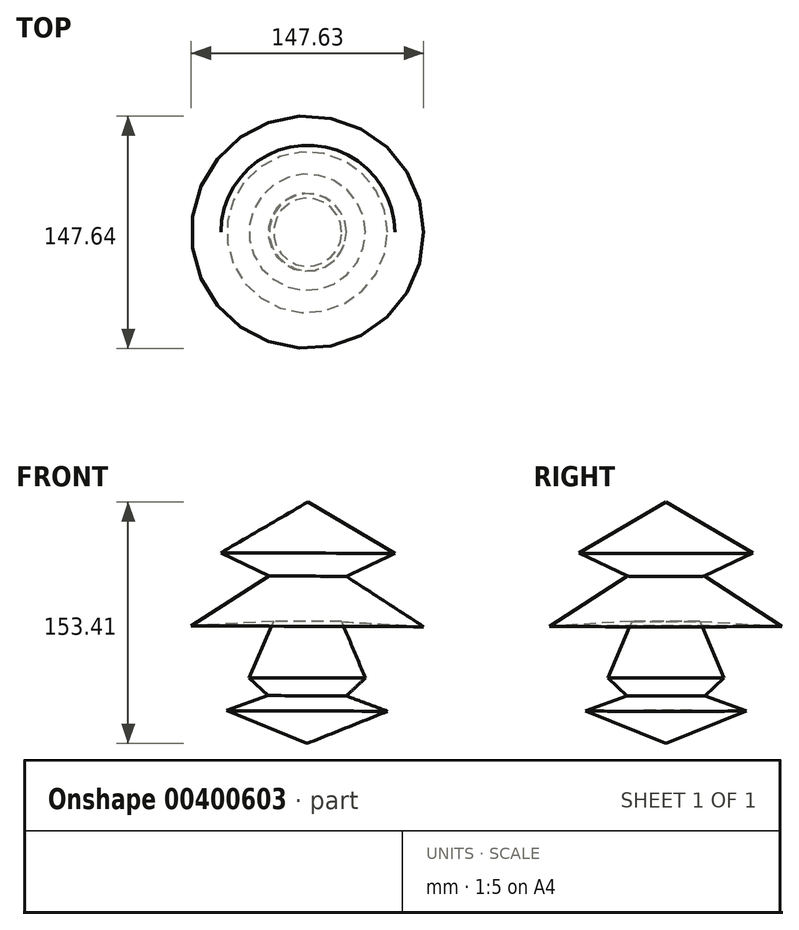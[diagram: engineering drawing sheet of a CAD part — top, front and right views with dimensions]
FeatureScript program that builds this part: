
annotation { "Feature Type Name" : "Feature", "Feature Type Description" : "" }
export const myFeature = defineFeature(function(context is Context, id is Id, definition is map)
    precondition{}
    {
        {
            var Q0;
            Q0=qCreatedBy(makeId("Front.planeOp"),FACE);
            var sketch = newSketch(context, id + "F0", { "sketchPlane" : qUnion([Q0])});
            skLineSegment(sketch, "E0", {"start": v(-14.32, 75.97) * mm, "end": v(40.82, 43.27) * mm});
            skLineSegment(sketch, "E1", {"start": v(40.82, 43.27) * mm, "end": v(9.99, 28.74) * mm});
            skLineSegment(sketch, "E2", {"start": v(9.99, 28.74) * mm, "end": v(59.2, -3.3) * mm});
            skLineSegment(sketch, "E3", {"start": v(59.2, -3.3) * mm, "end": v(7.03, 0) * mm});
            skLineSegment(sketch, "E4", {"start": v(7.03, 0) * mm, "end": v(22.14, -35.92) * mm});
            skLineSegment(sketch, "E5", {"start": v(22.14, -35.92) * mm, "end": v(9.99, -47.22) * mm});
            skLineSegment(sketch, "E6", {"start": v(9.99, -47.22) * mm, "end": v(38.15, -57.68) * mm});
            skLineSegment(sketch, "E7", {"start": v(36.25, -56.98) * mm, "end": v(-14.9, -77.44) * mm});
            skLineSegment(sketch, "E8", {"start": v(-14.32, 75.97) * mm, "end": v(-14.9, -77.44) * mm});
            skSolve(sketch);
        }
        {
            var Q0;
            Q0=makeQuery(id+"F0.imprint","IMPRINT",FACE,{"disambiguationData":[TD([[makeQuery(id+"F0.imprint","IMPRINT",EDGE,{"derivedFrom":sQuery(id+"F0.wireOp",EDGE,"E0")}),-1.0]])]});
            var Q1;
            Q1=sQuery(id+"F0.wireOp",EDGE,"E8");
            revolve(context, id + "F1", {"entities" : qUnion([Q0]), "axis" : qUnion([Q1]), "revolveType" : RevolveType.FULL});
        }
    });
